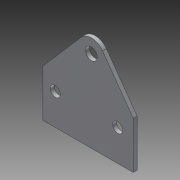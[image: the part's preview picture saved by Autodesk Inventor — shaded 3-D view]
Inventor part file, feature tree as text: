
AUTODESK INVENTOR PART (.ipt)
format: ipt  version: 2014 SP1 (Build 180222100, 222)  size: 96,768 bytes
history: native  units: in
note: dims shown in document units (in); Inventor stores cm internally (conversion verified against a paired STEP export)
features: extrude x2, sketch x2, reference x1
ambient origin geometry x8: Origin, YZ Plane, XZ Plane, XY Plane, X Axis, Y Axis, Z Axis, Center Point
bodies: Solid1 (feature_tree)
feature tree (5):
  extrude  "Extrusion1"  Depth=0.164in
  extrude  "Extrusion2"  Depth=1.0in
  sketch  "Sketch1"  dims[d0=0.164in d1=0.164in]
  reference  "Reference1"
  sketch  "Sketch2"  dims[d3=0.0625in d4=0.0in d5=0.5in d6=0.25in d7=0.2in d8=0.44in d9=0.25in d10=1.0in d11=0.19in d12=1.0in d13=0.0in]
